# Revit family: IS_LDV_T5408_BIM_NL
name_source: partatom
category: Plumbing Fixtures
units: mm (PartAtom-declared; Revit-internal decimal feet)

## family parameters
Cut with Voids When Loaded = No
Host = Face
OmniClass Number = 23.45.05.14.21
OmniClass Title = Bathtubs
Part Type = Normal
Room Calculation Point = No
Round Connector Dimension = Use Diameter
Shared = Yes

## types (1)
- T540801 - LDV TUB DUO 200X100 WHITE
    Accesoires = https://www.idealstandard.nl
    Accessories = https://www.idealstandard.nl
    Afmetingen = 2000 x 1000 x 464 mm
    AfstandsEenheid = millimeter
    Afwerking = Wit
    AreaUnits = millimeters
    Artikelnummer = T540801
    Artikelomschrijving = Ingebouwd bad van LDV 200x100 DUO, diepte 450 mm, rand van 3 cm
    Artikelreferentie = Ingebouwd bad van LDV 200x100 DUO, diepte 450 mm, rand van 3 cm NF-gecertificeerd, montagegebied aan de lange zijde boven de overloop. Alleen voor inbouwinstallatie.
    Assembly Code = C1030200
    AssetType = Fixed
    Auteur = Ideal Standard
    BIMObjectName = ISI_IdealStandard_Baths_LaDolceVita_T5408
    BREEAM = No
    BarCode = 8014140510147
    Barcode = 8014140510147
    BathType = Domestic
    Beschrijvinggarantie = fabrieksgarantie
    BimObjectNaam = ISI_IdealStandard_Baths_LaDolceVita_T5408
    Brand = Ideal Standard
    Breedte = 0
    BrutoGewicht = 0
    Category = SanitaryTerminal_BATH_UK
    Color = White
    ConnectionType = Plumbing
    CurrencyUnit = €
    Default Elevation = 1219 mm
    Description = Ingebouwd bad van LDV 200x100 DUO, diepte 450 mm, rand van 3 cm
    Diepte = 0 mm  [stored 0 ft]
    DrainSize = 52 mm
    DurationUnit = year
    DuurEenheid = Jaar
    ECA = No
    Eigenschappen = LDV TUB DUO 200X100 WHITE
    ExpectedLife = 30
    Features = Ingebouwd bad van LDV 200x100 DUO, diepte 450 mm, rand van 3 cm NF-gecertificeerd, montagegebied aan de lange zijde boven de overloop. Alleen voor inbouwinstallatie.
    Finish = Wit
    Garantieonderdelen = 25
    Garantieunits = Jaar
    GemaaktOp = 31-08-2023
    HasGrabHandles = No
    Help = https://www.idealstandard.nl
    Hoogte = 463,927967108434
    Hulp = https://www.idealstandard.nl
    IfcExportAs = IfcSanitaryTerminalType
    IfcExportType = BATH
    Installatieinstructies = https://www.idealstandard.nl
    InstallationInstructions = https://www.idealstandard.nl
    Kleur = Wit
    Lengte = 0 mm  [stored 0 ft]
    LinearUnits = millimeters
    Manufacturer = Ideal Standard
    ManufacturerURL = https://www.idealstandard.nl
    Materiaal = Acryl
    Material = Acryl
    MaterialThickness = 2 mm  [stored 0.00656168 ft]
    Merk = Ideal Standard
    Model = T540801
    ModelNumber = T540801
    ModelReference = Ingebouwd bad van LDV 200x100 DUO, diepte 450 mm, rand van 3 cm
    NBSDescription = Baths
    NBSReference = 45-35-70/311
    Name = ISI_Baths_LaDolceVita_T5408_IdealStandard
    NettWeight = Kg
    Nettogewicht = 0
    NominalDepth = 0 mm  [stored 0 ft]
    NominalHeight = 464 mm
    NominalLength = 2000 mm
    NominalWidth = 1000 mm
    OppervlakteEenheid = millimetre
    ProductInformation = https://www.idealstandard.nl
    ProductSoort = bad
    Productinformatie = https://www.idealstandard.nl
    Revisie = 1
    Shape = Rectangular
    Size = 2000 x 1000 x 464 mm
    Space = Internal
    SpareParts = https://www.idealstandard.nl
    TMV3 = No
    Telefoonnummer = 077 355 08 08
    Typeconnectie = loodgieter
    URL = https://www.idealstandard.nl
    Uniclass2 = Pr_40_20_06_08
    Uniclass2015Beschrijving = Baths
    Uniclass2015Code = Pr_40_20_06_08
    Uniclass2015Description = Baths
    Uniclass2015Reference = Pr_40_20_06_08 : Baths
    Uniclass2015Referentie = Pr_40_20_06_08
    Uniclass2015Title = Bathtubs; Tubs
    Uniclass2015Version = v1.31
    Urlproducent = https://www.idealstandard.nl
    ValutaEenheid = €
    Versie = 1
    Version = 1
    Vervangingskosten = 0
    VolumeUnits = Litres
    Volumeunits = Liter
    Vorm = rechthoekig
    WRAS = No
    WarrantyDescription = Manufacturers Warranty
    WarrantyDurationParts = 25
    WarrantyDurationUnit = year
    WarrantyGuarantorParts = https://www.idealstandard.nl
    WaterEfficientProduct = No
    Wisselstukken = https://www.idealstandard.nl

note: [stored X ft] marks values corroborated as IEEE doubles in the binary element streams (Revit-internal decimal feet)

## geometry (parser evidence)
native form markers: Blend x4, Sweep x2
no freeform markers — native parametric forms only
